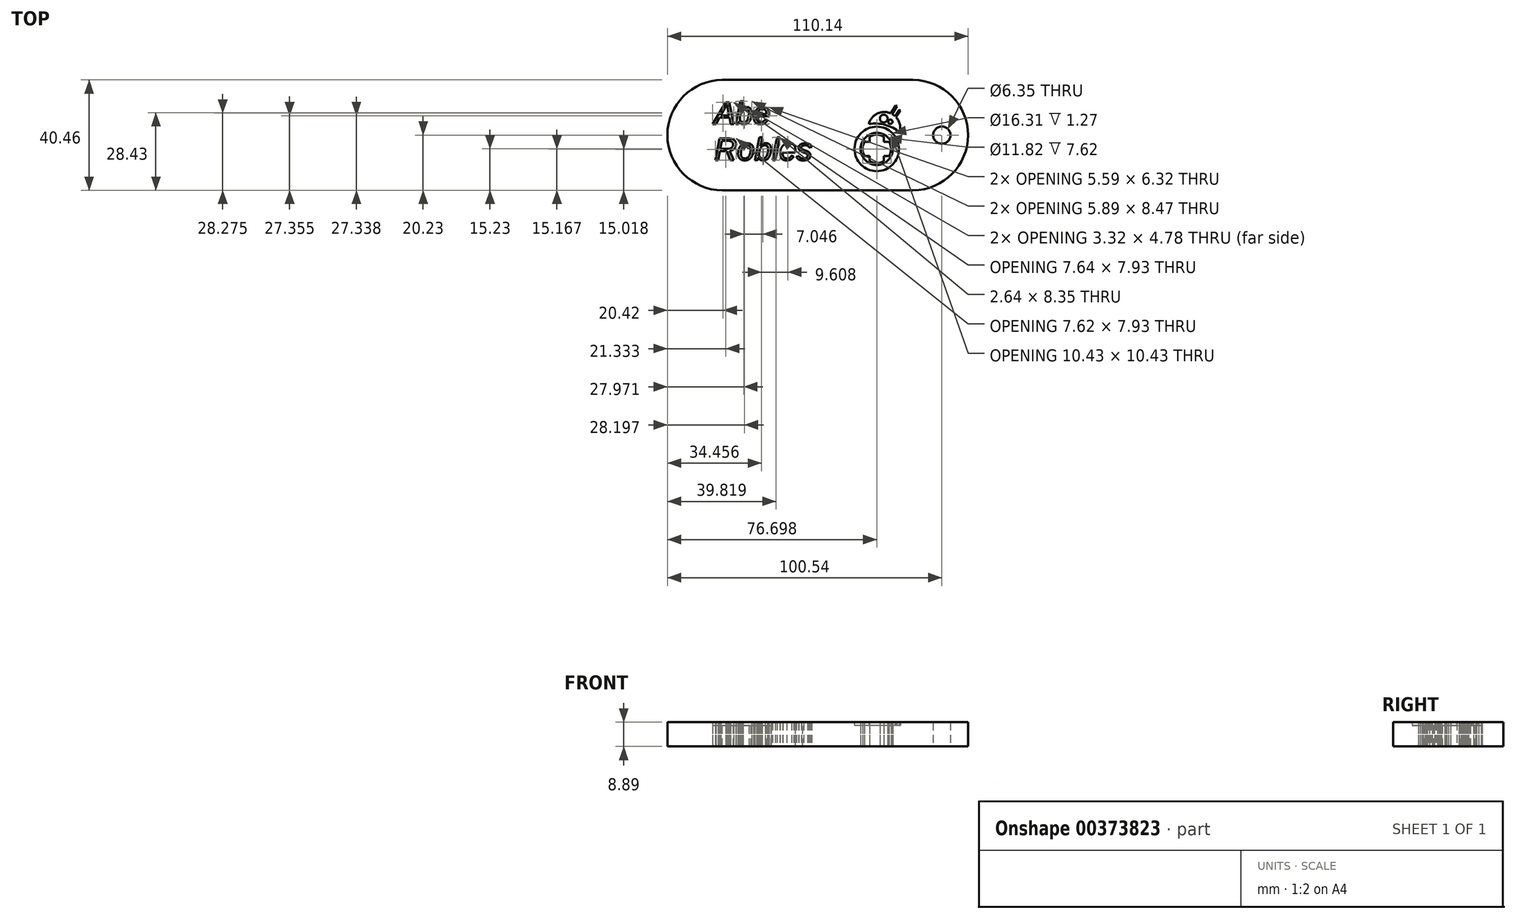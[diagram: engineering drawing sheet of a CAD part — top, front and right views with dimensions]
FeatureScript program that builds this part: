
annotation { "Feature Type Name" : "Feature", "Feature Type Description" : "" }
export const myFeature = defineFeature(function(context is Context, id is Id, definition is map)
    precondition{}
    {
        {
            var Q0;
            Q0=qCreatedBy(makeId("Top.planeOp"),FACE);
            var sketch = newSketch(context, id + "F0", { "sketchPlane" : qUnion([Q0])});
            skLineSegment(sketch, "E0.bottom", {"start": v(34.93, 20.23) * mm, "end": v(-34.93, 20.23) * mm});
            skLineSegment(sketch, "E0.top", {"start": v(34.93, -20.23) * mm, "end": v(-34.93, -20.23) * mm});
            skPoint(sketch, "E0.middle", {"position": v(0, 0) * mm});
            skArc(sketch, "E1", {"start": v(34.76, -20.23) * mm, "mid": v(55.07, 0) * mm, "end": v(34.76, 20.23) * mm});
            skPoint(sketch, "E1.third.point", {"position": v(55.07, 0) * mm});
            skArc(sketch, "E2.MirrorC", {"start": v(-34.76, -20.23) * mm, "mid": v(-55.07, 0) * mm, "end": v(-34.76, 20.23) * mm});
            skCircle(sketch, "E3", {"center": v(45.47, 0) * mm, "radius": 3.18 * mm});
            skText(sketch, "E4", { "text": "Abe \nRobles", "fontName": "Arimo-Italic.ttf"});
            skCircle(sketch, "E5", {"center": v(21.63, -5.06) * mm, "radius": 8.15 * mm});
            skArc(sketch, "E6", {"start": v(30.01, 1) * mm, "mid": v(30.07, 3.98) * mm, "end": v(28.66, 6.6) * mm});
            skArc(sketch, "E7", {"start": v(30.01, 1) * mm, "mid": v(24.7, 3.78) * mm, "end": v(18.72, 4.09) * mm});
            skCircle(sketch, "E8", {"center": v(24.2, 6.07) * mm, "radius": 1.42 * mm});
            skCircle(sketch, "E9", {"center": v(26.62, 4.88) * mm, "radius": 0.78 * mm});
            skLineSegment(sketch, "E10.bottom", {"start": v(29.02, 10.68) * mm, "end": v(28.56, 10.9) * mm});
            skLineSegment(sketch, "E10.left", {"start": v(29.02, 10.68) * mm, "end": v(27.25, 7.71) * mm});
            skLineSegment(sketch, "E10.right", {"start": v(28.56, 10.9) * mm, "end": v(26.8, 7.95) * mm});
            skPoint(sketch, "E10.middle", {"position": v(26.88, 7.9) * mm});
            skPoint(sketch, "E11.orphan", {"position": v(24.74, 5.13) * mm});
            skPoint(sketch, "E12.trimOffspring.end.orphan", {"position": v(25.2, 4.9) * mm});
            skArc(sketch, "E13.trimOffspring", {"start": v(26.8, 7.95) * mm, "mid": v(21.86, 7.9) * mm, "end": v(18.72, 4.09) * mm});
            skLineSegment(sketch, "E14.bottom", {"start": v(30.37, 8.96) * mm, "end": v(29.86, 9.2) * mm});
            skLineSegment(sketch, "E14.left", {"start": v(30.37, 8.96) * mm, "end": v(28.66, 6.6) * mm});
            skLineSegment(sketch, "E14.right", {"start": v(29.86, 9.2) * mm, "end": v(28.26, 7) * mm});
            skArc(sketch, "E15.trimOffspring", {"start": v(28.26, 7) * mm, "mid": v(27.77, 7.38) * mm, "end": v(27.25, 7.71) * mm});
            skCircle(sketch, "E16", {"center": v(21.63, -5.06) * mm, "radius": 5.9 * mm});
            skArc(sketch, "E17", {"start": v(17.1, -2.48) * mm, "mid": v(16.41, -5.06) * mm, "end": v(17.1, -7.65) * mm});
            skLineSegment(sketch, "E18.left", {"start": v(24.21, -0.53) * mm, "end": v(24.21, -2.48) * mm});
            skLineSegment(sketch, "E18.right", {"start": v(19.05, -0.53) * mm, "end": v(19.05, -2.48) * mm});
            skLineSegment(sketch, "E19.bottom", {"start": v(26.16, -2.48) * mm, "end": v(24.21, -2.48) * mm});
            skLineSegment(sketch, "E19.top", {"start": v(26.16, -7.65) * mm, "end": v(24.21, -7.65) * mm});
            skArc(sketch, "E20.trimOffspring", {"start": v(24.21, -0.53) * mm, "mid": v(21.63, 0.15) * mm, "end": v(19.05, -0.53) * mm});
            skArc(sketch, "E21.trimOffspring", {"start": v(26.16, -7.65) * mm, "mid": v(26.84, -5.06) * mm, "end": v(26.16, -2.48) * mm});
            skArc(sketch, "E22.trimOffspring", {"start": v(19.05, -9.6) * mm, "mid": v(21.63, -10.28) * mm, "end": v(24.21, -9.6) * mm});
            skLineSegment(sketch, "E23.trimOffspring", {"start": v(19.05, -7.65) * mm, "end": v(19.05, -9.6) * mm});
            skLineSegment(sketch, "E24.trimOffspring", {"start": v(24.21, -7.65) * mm, "end": v(24.21, -9.6) * mm});
            skLineSegment(sketch, "E25.trimOffspring", {"start": v(19.05, -2.48) * mm, "end": v(17.1, -2.48) * mm});
            skLineSegment(sketch, "E26.trimOffspring", {"start": v(19.05, -7.65) * mm, "end": v(17.1, -7.65) * mm});
            const initialGuessF0  = {"E4": [-0.0379, 0.00408, 1, 0, 0.0083]};
            skSetInitialGuess(sketch, initialGuessF0);
            skSolve(sketch);
        }
        {
            var Q0;
            Q0=makeQuery(id+"F0.imprint","IMPRINT",FACE,{"disambiguationData":[TD([[makeQuery(id+"F0.imprint","IMPRINT",EDGE,{"derivedFrom":sQuery(id+"F0.wireOp",EDGE,"E4.sketch_text.stroke-73")}),1.0]])]});
            var Q1;
            Q1=makeQuery(id+"F0.imprint","IMPRINT",FACE,{"disambiguationData":[TD([[makeQuery(id+"F0.imprint","IMPRINT",EDGE,{"derivedFrom":sQuery(id+"F0.wireOp",EDGE,"E4.sketch_text.stroke-91")}),1.0]])]});
            var Q2;
            Q2=makeQuery(id+"F0.imprint","IMPRINT",FACE,{"disambiguationData":[TD([[makeQuery(id+"F0.imprint","IMPRINT",EDGE,{"derivedFrom":sQuery(id+"F0.wireOp",EDGE,"E4.sketch_text.stroke-119")}),1.0]])]});
            var Q3;
            Q3=makeQuery(id+"F0.imprint","IMPRINT",FACE,{"disambiguationData":[TD([[makeQuery(id+"F0.imprint","IMPRINT",EDGE,{"derivedFrom":sQuery(id+"F0.wireOp",EDGE,"E4.sketch_text.stroke-58")}),1.0]])]});
            var Q4;
            Q4=makeQuery(id+"F0.imprint","IMPRINT",FACE,{"disambiguationData":[TD([[makeQuery(id+"F0.imprint","IMPRINT",EDGE,{"derivedFrom":sQuery(id+"F0.wireOp",EDGE,"E4.sketch_text.stroke-8")}),1.0]])]});
            var Q5;
            Q5=makeQuery(id+"F0.imprint","IMPRINT",FACE,{"disambiguationData":[TD([[makeQuery(id+"F0.imprint","IMPRINT",EDGE,{"derivedFrom":sQuery(id+"F0.wireOp",EDGE,"E4.sketch_text.stroke-27")}),1.0]])]});
            var Q6;
            Q6=makeQuery(id+"F0.imprint","IMPRINT",FACE,{"disambiguationData":[TD([[makeQuery(id+"F0.imprint","IMPRINT",EDGE,{"derivedFrom":sQuery(id+"F0.wireOp",EDGE,"E4.sketch_text.stroke-45")}),1.0]])]});
            var Q7;
            {var subQ1=sQuery(id+"F0.wireOp",EDGE,"E0.bottom");Q7=makeQuery(id+"F0.imprint","IMPRINT",FACE,{"disambiguationData":[TD([[makeQuery(id+"F0.imprint","IMPRINT",EDGE,{"derivedFrom":subQ1}),1.0]])]});}
            extrude(context, id + "F1", {"entities" : qUnion([Q0, Q1, Q2, Q3, Q4, Q5, Q6, Q7]), "depth" : 8.9 * mm});
        }
        {
            var Q0;
            Q0=makeQuery(id+"F0.imprint","IMPRINT",FACE,{"disambiguationData":[TD([[makeQuery(id+"F0.imprint","IMPRINT",EDGE,{"derivedFrom":sQuery(id+"F0.wireOp",EDGE,"E4.sketch_text.stroke-0")}),-1.0]])]});
            var Q1;
            Q1=makeQuery(id+"F0.imprint","IMPRINT",FACE,{"disambiguationData":[TD([[makeQuery(id+"F0.imprint","IMPRINT",EDGE,{"derivedFrom":sQuery(id+"F0.wireOp",EDGE,"E4.sketch_text.stroke-13")}),-1.0]])]});
            var Q2;
            Q2=makeQuery(id+"F0.imprint","IMPRINT",FACE,{"disambiguationData":[TD([[makeQuery(id+"F0.imprint","IMPRINT",EDGE,{"derivedFrom":sQuery(id+"F0.wireOp",EDGE,"E4.sketch_text.stroke-33")}),-1.0]])]});
            var Q3;
            Q3=makeQuery(id+"F0.imprint","IMPRINT",FACE,{"disambiguationData":[TD([[makeQuery(id+"F0.imprint","IMPRINT",EDGE,{"derivedFrom":sQuery(id+"F0.wireOp",EDGE,"E4.sketch_text.stroke-48")}),-1.0]])]});
            var Q4;
            Q4=makeQuery(id+"F0.imprint","IMPRINT",FACE,{"disambiguationData":[TD([[makeQuery(id+"F0.imprint","IMPRINT",EDGE,{"derivedFrom":sQuery(id+"F0.wireOp",EDGE,"E4.sketch_text.stroke-65")}),-1.0]])]});
            var Q5;
            Q5=makeQuery(id+"F0.imprint","IMPRINT",FACE,{"disambiguationData":[TD([[makeQuery(id+"F0.imprint","IMPRINT",EDGE,{"derivedFrom":sQuery(id+"F0.wireOp",EDGE,"E4.sketch_text.stroke-77")}),-1.0]])]});
            var Q6;
            Q6=makeQuery(id+"F0.imprint","IMPRINT",FACE,{"disambiguationData":[TD([[makeQuery(id+"F0.imprint","IMPRINT",EDGE,{"derivedFrom":sQuery(id+"F0.wireOp",EDGE,"E4.sketch_text.stroke-97")}),-1.0]])]});
            var Q7;
            Q7=makeQuery(id+"F0.imprint","IMPRINT",FACE,{"disambiguationData":[TD([[makeQuery(id+"F0.imprint","IMPRINT",EDGE,{"derivedFrom":sQuery(id+"F0.wireOp",EDGE,"E4.sketch_text.stroke-107")}),-1.0]])]});
            var Q8;
            Q8=makeQuery(id+"F0.imprint","IMPRINT",FACE,{"disambiguationData":[TD([[makeQuery(id+"F0.imprint","IMPRINT",EDGE,{"derivedFrom":sQuery(id+"F0.wireOp",EDGE,"E4.sketch_text.stroke-122")}),-1.0]])]});
            extrude(context, id + "F2", {"entities" : qUnion([Q0, Q1, Q2, Q3, Q4, Q5, Q6, Q7, Q8]), "depth" : 7.62 * mm});
        }
        {
            var Q0;
            Q0=makeQuery(id+"F0.imprint","IMPRINT",FACE,{"disambiguationData":[TD([[makeQuery(id+"F0.imprint","IMPRINT",EDGE,{"derivedFrom":sQuery(id+"F0.wireOp",EDGE,"E5")}),1.0]])]});
            var Q1;
            Q1=makeQuery(id+"F0.imprint","IMPRINT",FACE,{"disambiguationData":[TD([[makeQuery(id+"F0.imprint","IMPRINT",EDGE,{"derivedFrom":sQuery(id+"F0.wireOp",EDGE,"E6")}),1.0]])]});
            var Q2;
            Q2=makeQuery(id+"F0.imprint","IMPRINT",FACE,{"disambiguationData":[TD([[makeQuery(id+"F0.imprint","IMPRINT",EDGE,{"derivedFrom":sQuery(id+"F0.wireOp",EDGE,"E17")}),1.0]])]});
            extrude(context, id + "F3", {"entities" : qUnion([Q0, Q1, Q2]), "operationType" : NewBodyOperationType.ADD, "depth" : 7.62 * mm});
        }
        {
            var Q0;
            Q0=makeQuery(id+"F0.imprint","IMPRINT",FACE,{"disambiguationData":[TD([[makeQuery(id+"F0.imprint","IMPRINT",EDGE,{"derivedFrom":sQuery(id+"F0.wireOp",EDGE,"E16")}),1.0]])]});
            var Q1;
            Q1=makeQuery(id+"F0.imprint","IMPRINT",FACE,{"disambiguationData":[TD([[makeQuery(id+"F0.imprint","IMPRINT",EDGE,{"derivedFrom":sQuery(id+"F0.wireOp",EDGE,"E9")}),1.0]])]});
            var Q2;
            Q2=makeQuery(id+"F0.imprint","IMPRINT",FACE,{"disambiguationData":[TD([[makeQuery(id+"F0.imprint","IMPRINT",EDGE,{"derivedFrom":sQuery(id+"F0.wireOp",EDGE,"E8")}),1.0]])]});
            extrude(context, id + "F4", {"entities" : qUnion([Q0, Q1, Q2]), "depth" : 8.9 * mm});
        }
    });
